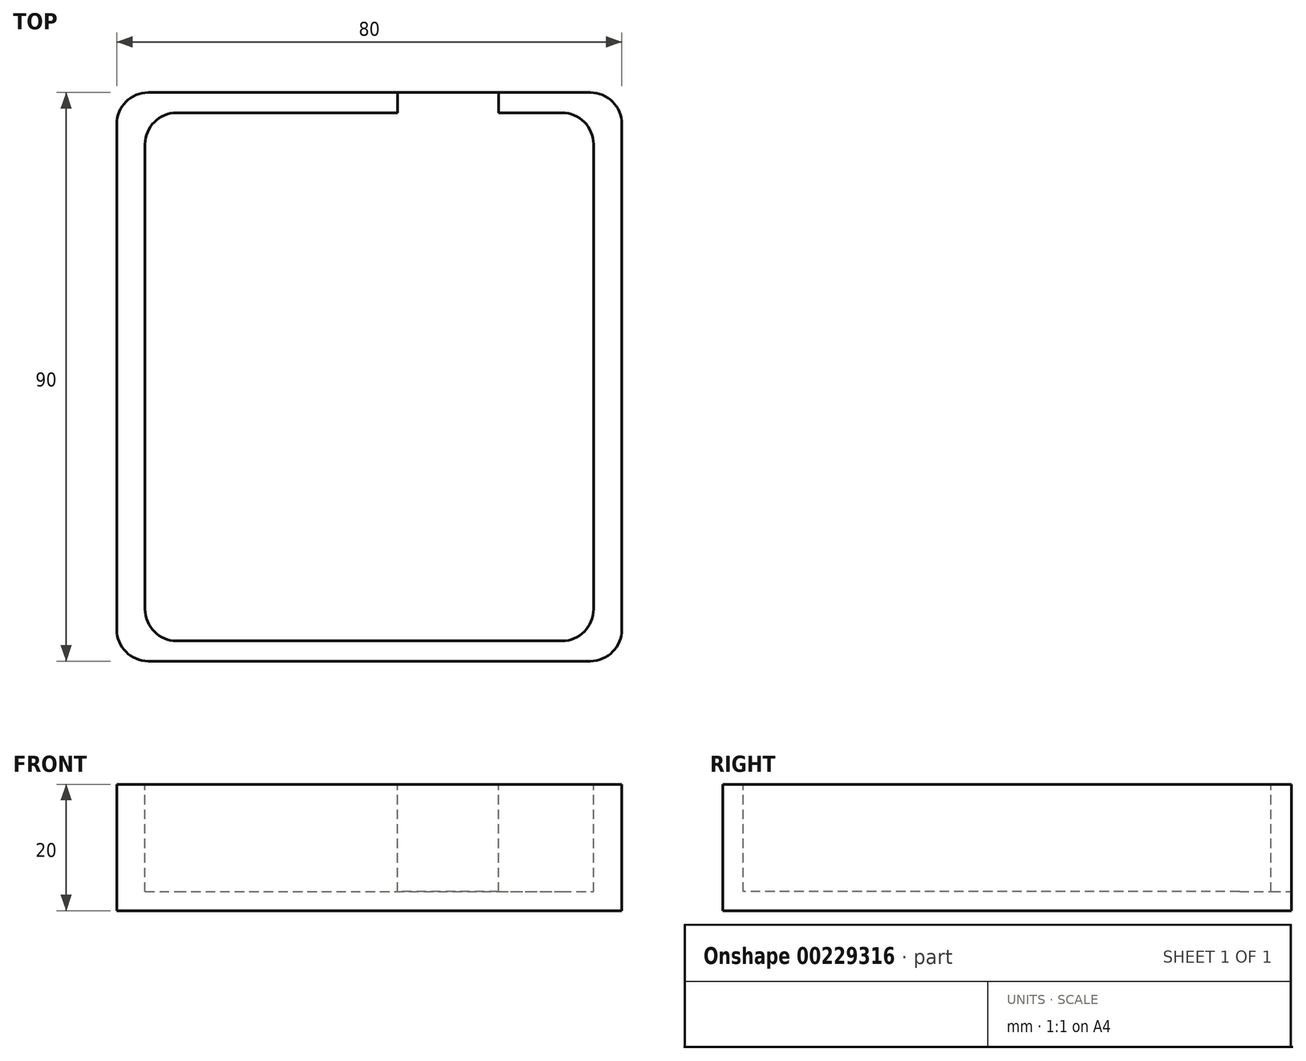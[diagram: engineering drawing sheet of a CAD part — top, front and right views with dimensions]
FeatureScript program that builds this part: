
annotation { "Feature Type Name" : "Feature", "Feature Type Description" : "" }
export const myFeature = defineFeature(function(context is Context, id is Id, definition is map)
    precondition{}
    {
        {
            var Q0;
            Q0=qCreatedBy(makeId("Top.planeOp"),FACE);
            var sketch = newSketch(context, id + "F0", { "sketchPlane" : qUnion([Q0])});
            skLineSegment(sketch, "E0.bottom", {"start": v(-40, 45) * mm, "end": v(40, 45) * mm});
            skLineSegment(sketch, "E0.top", {"start": v(-40, -45) * mm, "end": v(40, -45) * mm});
            skLineSegment(sketch, "E0.left", {"start": v(-40, 45) * mm, "end": v(-40, -45) * mm});
            skLineSegment(sketch, "E0.right", {"start": v(40, 45) * mm, "end": v(40, -45) * mm});
            skPoint(sketch, "E1", {"position": v(0, 45) * mm});
            skPoint(sketch, "E2", {"position": v(-40, 0) * mm});
            skSolve(sketch);
        }
        {
            var Q0;
            Q0=makeQuery(id+"F0.imprint","IMPRINT",FACE,{"disambiguationData":[TD([[makeQuery(id+"F0.imprint","IMPRINT",EDGE,{"derivedFrom":sQuery(id+"F0.wireOp",EDGE,"E0.bottom")}),-1.0]])]});
            extrude(context, id + "F1", {"entities" : qUnion([Q0]), "depth" : 20 * mm});
        }
        {
            var Q0;
            Q0=makeQuery(id+"F1.opExtrude","CAP_FACE",FACE,{"disambiguationData":[OSD([sQuery(id+"F0.wireOp",EDGE,"E0.bottom"),sQuery(id+"F0.wireOp",EDGE,"E0.top"),sQuery(id+"F0.wireOp",EDGE,"E0.left"),sQuery(id+"F0.wireOp",EDGE,"E0.right")])],"isStart":false});
            var sketch = newSketch(context, id + "F2", { "sketchPlane" : qUnion([Q0])});
            skLineSegment(sketch, "E3.bottom", {"start": v(-35.5, 41.8) * mm, "end": v(35.5, 41.8) * mm});
            skLineSegment(sketch, "E3.top", {"start": v(-35.5, -41.8) * mm, "end": v(35.5, -41.8) * mm});
            skLineSegment(sketch, "E3.left", {"start": v(-35.5, 41.8) * mm, "end": v(-35.5, -41.8) * mm});
            skLineSegment(sketch, "E3.right", {"start": v(35.5, 41.8) * mm, "end": v(35.5, -41.8) * mm});
            skPoint(sketch, "E4", {"position": v(0, 41.8) * mm});
            skPoint(sketch, "E5", {"position": v(35.5, 0) * mm});
            skSolve(sketch);
        }
        {
            var Q0;
            Q0=makeQuery(id+"F2.imprint","IMPRINT",FACE,{"disambiguationData":[TD([[makeQuery(id+"F2.imprint","IMPRINT",EDGE,{"derivedFrom":sQuery(id+"F2.wireOp",EDGE,"E3.bottom")}),-1.0]])]});
            extrude(context, id + "F3", {"entities" : qUnion([Q0]), "operationType" : NewBodyOperationType.REMOVE, "oppositeDirection" : true, "depth" : 17 * mm});
        }
        {
            var Q0;
            Q0=makeQuery(id+"F1.opExtrude","CAP_FACE",FACE,{"disambiguationData":[OSD([sQuery(id+"F0.wireOp",EDGE,"E0.bottom"),sQuery(id+"F0.wireOp",EDGE,"E0.top"),sQuery(id+"F0.wireOp",EDGE,"E0.left"),sQuery(id+"F0.wireOp",EDGE,"E0.right")])],"isStart":false});
            var sketch = newSketch(context, id + "F4", { "sketchPlane" : qUnion([Q0])});
            skLineSegment(sketch, "E6.bottom", {"start": v(4.5, 45) * mm, "end": v(20.5, 45) * mm});
            skLineSegment(sketch, "E6.top", {"start": v(4.5, 41.8) * mm, "end": v(20.5, 41.8) * mm});
            skLineSegment(sketch, "E6.left", {"start": v(4.5, 45) * mm, "end": v(4.5, 41.8) * mm});
            skLineSegment(sketch, "E6.right", {"start": v(20.5, 45) * mm, "end": v(20.5, 41.8) * mm});
            skSolve(sketch);
        }
        {
            var Q0;
            Q0=makeQuery(id+"F4.imprint","IMPRINT",FACE,{"disambiguationData":[TD([[makeQuery(id+"F4.imprint","IMPRINT",EDGE,{"derivedFrom":sQuery(id+"F4.wireOp",EDGE,"E6.bottom")}),-1.0]])]});
            var Q1;
            Q1=makeQuery(id+"F3.boolean.opBoolean","COPY",FACE,{"derivedFrom":makeQuery(id+"F3.opExtrude","CAP_FACE",FACE,{"disambiguationData":[OSD([sQuery(id+"F2.wireOp",EDGE,"E3.bottom"),sQuery(id+"F2.wireOp",EDGE,"E3.top"),sQuery(id+"F2.wireOp",EDGE,"E3.left"),sQuery(id+"F2.wireOp",EDGE,"E3.right")])],"isStart":false})});
            extrude(context, id + "F5", {"entities" : qUnion([Q0]), "operationType" : NewBodyOperationType.REMOVE, "endBound" : BoundingType.UP_TO_SURFACE, "oppositeDirection" : true, "endBoundEntityFace" : qUnion([Q1]), "depth" : 25 * mm});
        }
        {
            var Q0;
            Q0=makeQuery(id+"F1.opExtrude","SWEPT_EDGE",EDGE,{"disambiguationData":[OSD([sQuery(id+"F0.wireOp",EDGE,"E0.bottom"),sQuery(id+"F0.wireOp",EDGE,"E0.right")])]});
            var Q1;
            Q1=makeQuery(id+"F1.opExtrude","SWEPT_EDGE",EDGE,{"disambiguationData":[OSD([sQuery(id+"F0.wireOp",EDGE,"E0.top"),sQuery(id+"F0.wireOp",EDGE,"E0.right")])]});
            var Q2;
            Q2=makeQuery(id+"F1.opExtrude","SWEPT_EDGE",EDGE,{"disambiguationData":[OSD([sQuery(id+"F0.wireOp",EDGE,"E0.top"),sQuery(id+"F0.wireOp",EDGE,"E0.left")])]});
            var Q3;
            Q3=makeQuery(id+"F1.opExtrude","SWEPT_EDGE",EDGE,{"disambiguationData":[OSD([sQuery(id+"F0.wireOp",EDGE,"E0.bottom"),sQuery(id+"F0.wireOp",EDGE,"E0.left")])]});
            fillet(context, id + "F6", {"entities" : qUnion([Q0, Q1, Q2, Q3]), "radius" : 5 * mm, "tangentPropagation" : true, "allowEdgeOverflow" : false});
        }
        {
            var Q0;
            Q0=makeQuery(id+"F3.boolean.opBoolean","COPY",EDGE,{"derivedFrom":makeQuery(id+"F3.opExtrude","SWEPT_EDGE",EDGE,{"disambiguationData":[OSD([sQuery(id+"F2.wireOp",EDGE,"E3.top"),sQuery(id+"F2.wireOp",EDGE,"E3.right")])]})});
            var Q1;
            Q1=makeQuery(id+"F3.boolean.opBoolean","COPY",EDGE,{"derivedFrom":makeQuery(id+"F3.opExtrude","SWEPT_EDGE",EDGE,{"disambiguationData":[OSD([sQuery(id+"F2.wireOp",EDGE,"E3.bottom"),sQuery(id+"F2.wireOp",EDGE,"E3.right")])]})});
            var Q2;
            Q2=makeQuery(id+"F3.boolean.opBoolean","COPY",EDGE,{"derivedFrom":makeQuery(id+"F3.opExtrude","SWEPT_EDGE",EDGE,{"disambiguationData":[OSD([sQuery(id+"F2.wireOp",EDGE,"E3.bottom"),sQuery(id+"F2.wireOp",EDGE,"E3.left")])]})});
            var Q3;
            Q3=makeQuery(id+"F3.boolean.opBoolean","COPY",EDGE,{"derivedFrom":makeQuery(id+"F3.opExtrude","SWEPT_EDGE",EDGE,{"disambiguationData":[OSD([sQuery(id+"F2.wireOp",EDGE,"E3.top"),sQuery(id+"F2.wireOp",EDGE,"E3.left")])]})});
            fillet(context, id + "F7", {"entities" : qUnion([Q0, Q1, Q2, Q3]), "radius" : 5 * mm, "tangentPropagation" : true, "allowEdgeOverflow" : false});
        }
    });
